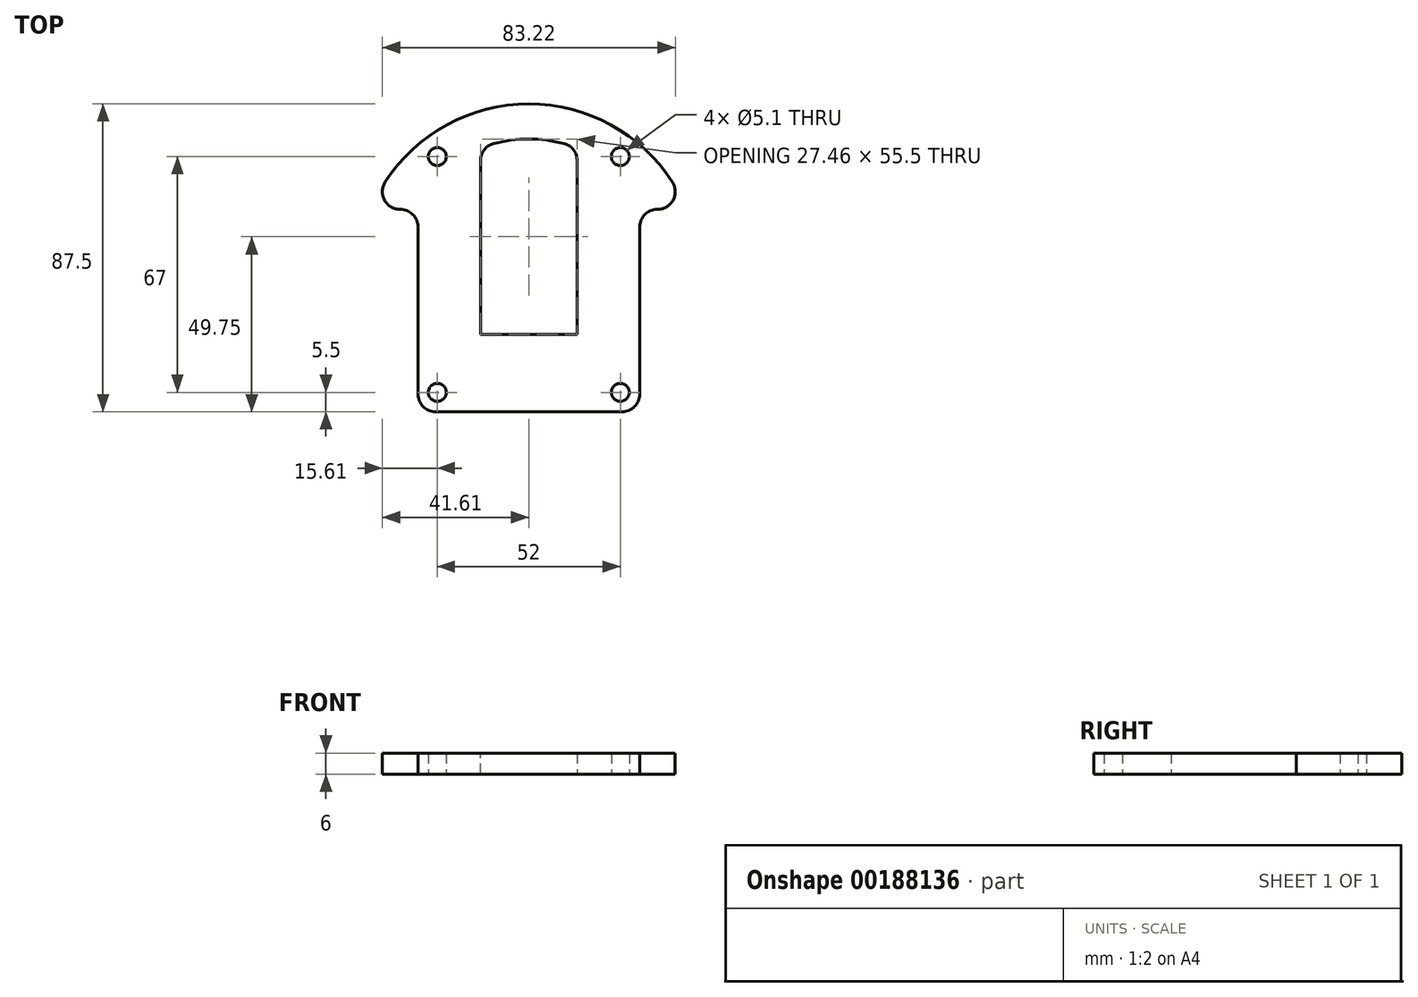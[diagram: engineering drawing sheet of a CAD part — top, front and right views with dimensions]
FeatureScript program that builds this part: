
annotation { "Feature Type Name" : "Feature", "Feature Type Description" : "" }
export const myFeature = defineFeature(function(context is Context, id is Id, definition is map)
    precondition{}
    {
        {
            var Q0;
            Q0=qCreatedBy(makeId("Top.planeOp"),FACE);
            var sketch = newSketch(context, id + "F0", { "sketchPlane" : qUnion([Q0])});
            skLineSegment(sketch, "E0.bottom", {"start": v(-26.5, 39) * mm, "end": v(26.5, 39) * mm});
            skLineSegment(sketch, "E0.top", {"start": v(-26.5, -39) * mm, "end": v(26.5, -39) * mm});
            skLineSegment(sketch, "E0.left", {"start": v(-31.5, 34) * mm, "end": v(-31.5, -34) * mm});
            skLineSegment(sketch, "E0.right", {"start": v(31.5, 34) * mm, "end": v(31.5, -34) * mm});
            skLineSegment(sketch, "E1", {"start": v(-31.5, -39) * mm, "end": v(31.5, 39) * mm, "construction": true});
            skLineSegment(sketch, "E2.bottom", {"start": v(-13.73, 17) * mm, "end": v(13.73, 17) * mm});
            skLineSegment(sketch, "E2.top", {"start": v(-13.73, -17) * mm, "end": v(13.73, -17) * mm});
            skLineSegment(sketch, "E2.left", {"start": v(-13.73, 17) * mm, "end": v(-13.73, -17) * mm});
            skLineSegment(sketch, "E2.right", {"start": v(13.73, 17) * mm, "end": v(13.73, -17) * mm});
            skCircle(sketch, "E3", {"center": v(-26, 33.5) * mm, "radius": 2.55 * mm});
            skCircle(sketch, "E4", {"center": v(26, 33.5) * mm, "radius": 2.55 * mm});
            skCircle(sketch, "E5", {"center": v(-26, -33.5) * mm, "radius": 2.55 * mm});
            skCircle(sketch, "E6", {"center": v(26, -33.5) * mm, "radius": 2.55 * mm});
            skLineSegment(sketch, "E7.bottom", {"start": v(-26, 33.5) * mm, "end": v(26, 33.5) * mm, "construction": true});
            skLineSegment(sketch, "E7.top", {"start": v(-26, -33.5) * mm, "end": v(26, -33.5) * mm, "construction": true});
            skLineSegment(sketch, "E7.left", {"start": v(-26, 33.5) * mm, "end": v(-26, -33.5) * mm, "construction": true});
            skLineSegment(sketch, "E7.right", {"start": v(26, 33.5) * mm, "end": v(26, -33.5) * mm, "construction": true});
            skLineSegment(sketch, "E8", {"start": v(-26, 33.5) * mm, "end": v(26, -33.5) * mm, "construction": true});
            skPoint(sketch, "E9.visualSharp", {"position": v(-31.5, 39) * mm});
            skArc(sketch, "E9.filletArc", {"start": v(-26.5, 39) * mm, "mid": v(-30.04, 37.54) * mm, "end": v(-31.5, 34) * mm});
            skPoint(sketch, "E10.visualSharp", {"position": v(31.5, 39) * mm});
            skArc(sketch, "E10.filletArc", {"start": v(31.5, 34) * mm, "mid": v(30.04, 37.54) * mm, "end": v(26.5, 39) * mm});
            skPoint(sketch, "E11.visualSharp", {"position": v(-31.5, -39) * mm});
            skArc(sketch, "E11.filletArc", {"start": v(-31.5, -34) * mm, "mid": v(-30.04, -37.54) * mm, "end": v(-26.5, -39) * mm});
            skPoint(sketch, "E12.visualSharp", {"position": v(31.5, -39) * mm});
            skArc(sketch, "E12.filletArc", {"start": v(26.5, -39) * mm, "mid": v(30.04, -37.54) * mm, "end": v(31.5, -34) * mm});
            skSolve(sketch);
        }
        {
            var Q0;
            Q0 = qSketchRegion(id + "F0", true);
            extrude(context, id + "F1", {"entities" : qUnion([Q0]), "depth" : 6 * mm});
        }
        {
            var Q0;
            Q0=qCreatedBy(makeId("Top.planeOp"),FACE);
            var sketch = newSketch(context, id + "F2", { "sketchPlane" : qUnion([Q0])});
            skCircle(sketch, "E13", {"center": v(0, 0) * mm, "radius": 49.5 * mm, "construction": true});
            skCircle(sketch, "E14", {"center": v(-40, 0) * mm, "radius": 9.5 * mm, "construction": true});
            skCircle(sketch, "E15", {"center": v(40, 0) * mm, "radius": 9.5 * mm, "construction": true});
            skArc(sketch, "E16.0", {"start": v(44.83, 18.5) * mm, "mid": v(0, 48.5) * mm, "end": v(-44.83, 18.5) * mm});
            skLineSegment(sketch, "E17", {"start": v(-44.83, 18.5) * mm, "end": v(44.83, 18.5) * mm});
            skCircle(sketch, "E18.0", {"center": v(-26, 33.5) * mm, "radius": 2.55 * mm});
            skCircle(sketch, "E18.1", {"center": v(26, 33.5) * mm, "radius": 2.55 * mm});
            skSolve(sketch);
        }
        {
            var Q0;
            Q0 = qSketchRegion(id + "F2", true);
            var Q1;
            Q1=makeQuery(id+"F1.opExtrude","CAP_FACE",FACE,{"disambiguationData":[OSD([sQuery(id+"F0.wireOp",EDGE,"E0.bottom"),sQuery(id+"F0.wireOp",EDGE,"E0.top"),sQuery(id+"F0.wireOp",EDGE,"E0.left"),sQuery(id+"F0.wireOp",EDGE,"E0.right"),sQuery(id+"F0.wireOp",EDGE,"E2.bottom"),sQuery(id+"F0.wireOp",EDGE,"E2.top"),sQuery(id+"F0.wireOp",EDGE,"E2.left"),sQuery(id+"F0.wireOp",EDGE,"E2.right"),sQuery(id+"F0.wireOp",EDGE,"E3"),sQuery(id+"F0.wireOp",EDGE,"E4"),sQuery(id+"F0.wireOp",EDGE,"E5"),sQuery(id+"F0.wireOp",EDGE,"E6")])],"isStart":false});
            extrude(context, id + "F3", {"entities" : qUnion([Q0]), "operationType" : NewBodyOperationType.ADD, "endBound" : BoundingType.UP_TO_SURFACE, "endBoundEntityFace" : qUnion([Q1]), "depth" : 25 * mm});
        }
        {
            var Q0;
            Q0=qCreatedBy(makeId("Top.planeOp"),FACE);
            var sketch = newSketch(context, id + "F4", { "sketchPlane" : qUnion([Q0])});
            skArc(sketch, "E19.0", {"start": v(44.83, 18.5) * mm, "mid": v(0, 48.5) * mm, "end": v(-44.83, 18.5) * mm, "construction": true});
            skArc(sketch, "E20.0", {"start": v(13.73, 35.97) * mm, "mid": v(0, 38.5) * mm, "end": v(-13.73, 35.97) * mm});
            skLineSegment(sketch, "E21", {"start": v(-13.73, 35.97) * mm, "end": v(-13.73, 17) * mm});
            skLineSegment(sketch, "E22", {"start": v(-13.73, 17) * mm, "end": v(13.73, 17) * mm});
            skLineSegment(sketch, "E23", {"start": v(13.73, 17) * mm, "end": v(13.73, 35.97) * mm});
            skSolve(sketch);
        }
        {
            var Q0;
            Q0 = qSketchRegion(id + "F4", true);
            extrude(context, id + "F5", {"entities" : qUnion([Q0]), "operationType" : NewBodyOperationType.REMOVE, "endBound" : BoundingType.THROUGH_ALL, "depth" : 25 * mm});
        }
        {
            var Q0;
            {var subQ0=sQuery(id+"F2.wireOp",EDGE,"E17");var subQ1=sQuery(id+"F2.wireOp",EDGE,"E16.0");Q0=makeQuery(id+"F3.opExtrude","SWEPT_EDGE",EDGE,{"disambiguationData":[OSD([subQ1,subQ0]),TDD([makeQuery(id+"F2.imprint","INTERSECT",VERTEX,{"disambiguationData":[OD(1.0)],"derivedFrom":[subQ1,subQ0]})])]});}
            var Q1;
            Q1=makeQuery(id+"F3.boolean.opBoolean","INTERSECT",EDGE,{"derivedFrom":[makeQuery(id+"F1.opExtrude","SWEPT_FACE",FACE,{"disambiguationData":[OSD([sQuery(id+"F0.wireOp",EDGE,"E0.left")])]}),makeQuery(id+"F3.opExtrude","SWEPT_FACE",FACE,{"disambiguationData":[OSD([sQuery(id+"F2.wireOp",EDGE,"E17")])]})]});
            var Q2;
            {var subQ0=sQuery(id+"F2.wireOp",EDGE,"E17");var subQ1=sQuery(id+"F2.wireOp",EDGE,"E16.0");Q2=makeQuery(id+"F3.opExtrude","SWEPT_EDGE",EDGE,{"disambiguationData":[OSD([subQ1,subQ0]),TDD([makeQuery(id+"F2.imprint","INTERSECT",VERTEX,{"disambiguationData":[OD(0.0)],"derivedFrom":[subQ1,subQ0]})])]});}
            var Q3;
            Q3=makeQuery(id+"F3.boolean.opBoolean","INTERSECT",EDGE,{"derivedFrom":[makeQuery(id+"F1.opExtrude","SWEPT_FACE",FACE,{"disambiguationData":[OSD([sQuery(id+"F0.wireOp",EDGE,"E0.right")])]}),makeQuery(id+"F3.opExtrude","SWEPT_FACE",FACE,{"disambiguationData":[OSD([sQuery(id+"F2.wireOp",EDGE,"E17")])]})]});
            var Q4;
            Q4=makeQuery(id+"F5.boolean.opBoolean","COPY",EDGE,{"derivedFrom":makeQuery(id+"F5.opExtrude","SWEPT_EDGE",EDGE,{"disambiguationData":[OSD([sQuery(id+"F4.wireOp",EDGE,"E20.0"),sQuery(id+"F4.wireOp",EDGE,"E23")])]})});
            var Q5;
            Q5=makeQuery(id+"F5.boolean.opBoolean","COPY",EDGE,{"derivedFrom":makeQuery(id+"F5.opExtrude","SWEPT_EDGE",EDGE,{"disambiguationData":[OSD([sQuery(id+"F4.wireOp",EDGE,"E20.0"),sQuery(id+"F4.wireOp",EDGE,"E21")])]})});
            fillet(context, id + "F6", {"entities" : qUnion([Q0, Q1, Q2, Q3, Q4, Q5]), "radius" : 5 * mm, "tangentPropagation" : true, "allowEdgeOverflow" : false});
        }
    });
